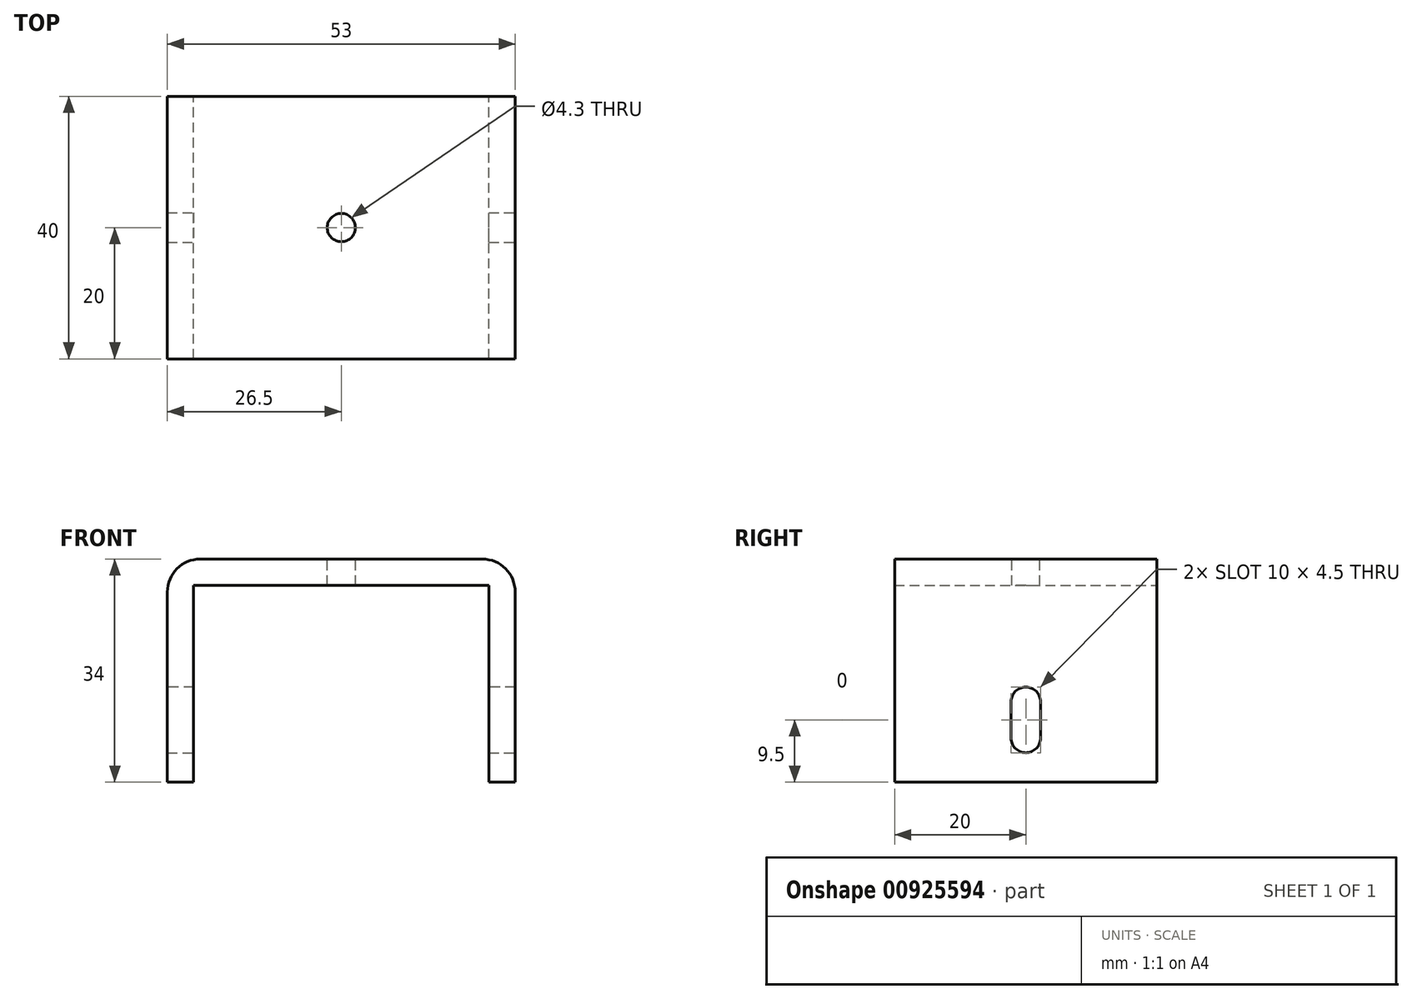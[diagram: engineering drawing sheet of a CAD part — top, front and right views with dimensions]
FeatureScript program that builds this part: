
annotation { "Feature Type Name" : "Feature", "Feature Type Description" : "" }
export const myFeature = defineFeature(function(context is Context, id is Id, definition is map)
    precondition{}
    {
        {
            var Q0;
            Q0=qCreatedBy(makeId("Front.planeOp"),FACE);
            var sketch = newSketch(context, id + "F0", { "sketchPlane" : qUnion([Q0])});
            skLineSegment(sketch, "E0.bottom", {"start": v(26.5, -17) * mm, "end": v(22.5, -17) * mm});
            skLineSegment(sketch, "E0.top", {"start": v(26.5, 17) * mm, "end": v(-26.5, 17) * mm});
            skLineSegment(sketch, "E0.left", {"start": v(26.5, -17) * mm, "end": v(26.5, 17) * mm});
            skLineSegment(sketch, "E0.right", {"start": v(-26.5, -17) * mm, "end": v(-26.5, 17) * mm});
            skPoint(sketch, "E0.middle", {"position": v(0, 0) * mm});
            skLineSegment(sketch, "E1.0", {"start": v(22.5, -17) * mm, "end": v(22.5, 13) * mm});
            skLineSegment(sketch, "E1.1", {"start": v(22.5, 13) * mm, "end": v(-22.5, 13) * mm});
            skLineSegment(sketch, "E1.2", {"start": v(-22.5, -17) * mm, "end": v(-22.5, 13) * mm});
            skLineSegment(sketch, "E2.trimOffspring", {"start": v(-22.5, -17) * mm, "end": v(-26.5, -17) * mm});
            skSolve(sketch);
        }
        {
            var Q0;
            Q0 = qSketchRegion(id + "F0", true);
            extrude(context, id + "F1", {"entities" : qUnion([Q0]), "depth" : 40 * mm, "offsetDistance" : 25 * mm});
        }
        {
            var Q0;
            Q0=makeQuery(id+"F1.opExtrude","SWEPT_EDGE",EDGE,{"disambiguationData":[OSD([sQuery(id+"F0.wireOp",EDGE,"E0.top"),sQuery(id+"F0.wireOp",EDGE,"E0.right")])]});
            var Q1;
            Q1=makeQuery(id+"F1.opExtrude","SWEPT_EDGE",EDGE,{"disambiguationData":[OSD([sQuery(id+"F0.wireOp",EDGE,"E0.top"),sQuery(id+"F0.wireOp",EDGE,"E0.left")])]});
            fillet(context, id + "F2", {"entities" : qUnion([Q0, Q1]), "radius" : 5 * mm, "tangentPropagation" : true, "allowEdgeOverflow" : false});
        }
        {
            var Q0;
            Q0=makeQuery(id+"F1.opExtrude","SWEPT_FACE",FACE,{"disambiguationData":[OSD([sQuery(id+"F0.wireOp",EDGE,"E0.top")])]});
            var sketch = newSketch(context, id + "F3", { "sketchPlane" : qUnion([Q0])});
            skCircle(sketch, "E3", {"center": v(0, -20) * mm, "radius": 2.15 * mm});
            skPoint(sketch, "E3.centerSnap0", {"position": v(21.5, -20) * mm});
            skSolve(sketch);
        }
        {
            var Q0;
            Q0 = qSketchRegion(id + "F3", true);
            extrude(context, id + "F4", {"entities" : qUnion([Q0]), "operationType" : NewBodyOperationType.REMOVE, "oppositeDirection" : true, "depth" : 25 * mm, "offsetDistance" : 25 * mm});
        }
        {
            var Q0;
            Q0=makeQuery(id+"F1.opExtrude","SWEPT_FACE",FACE,{"disambiguationData":[OSD([sQuery(id+"F0.wireOp",EDGE,"E0.left")])]});
            var sketch = newSketch(context, id + "F5", { "sketchPlane" : qUnion([Q0])});
            skLineSegment(sketch, "E4.bottom", {"start": v(-17.75, -12.5) * mm, "end": v(-22.25, -12.5) * mm});
            skLineSegment(sketch, "E4.top", {"start": v(-17.75, -2.5) * mm, "end": v(-22.25, -2.5) * mm});
            skLineSegment(sketch, "E4.left", {"start": v(-17.75, -12.5) * mm, "end": v(-17.75, -2.5) * mm});
            skLineSegment(sketch, "E4.right", {"start": v(-22.25, -12.5) * mm, "end": v(-22.25, -2.5) * mm});
            skPoint(sketch, "E4.middle", {"position": v(-20, -7.5) * mm});
            skPoint(sketch, "E4.middle.positionSnap0", {"position": v(-20, -17) * mm});
            skPoint(sketch, "E4.centerSnap0", {"position": v(-20, -17) * mm});
            skSolve(sketch);
        }
        {
            var Q0;
            Q0 = qSketchRegion(id + "F5", true);
            extrude(context, id + "F6", {"entities" : qUnion([Q0]), "operationType" : NewBodyOperationType.REMOVE, "endBound" : BoundingType.THROUGH_ALL, "oppositeDirection" : true, "depth" : 25 * mm, "offsetDistance" : 25 * mm});
        }
        {
            var Q0;
            {var subQ0=sQuery(id+"F5.wireOp",EDGE,"E4.top");var subQ1=sQuery(id+"F5.wireOp",EDGE,"E4.left");Q0=makeQuery(id+"F6.boolean.opBoolean","COPY",EDGE,{"disambiguationData":[TD([makeQuery(id+"F1.opExtrude","SWEPT_FACE",FACE,{"disambiguationData":[OSD([sQuery(id+"F0.wireOp",EDGE,"E0.left")])]})])],"derivedFrom":makeQuery(id+"F6.opExtrude","SWEPT_EDGE",EDGE,{"disambiguationData":[OSD([subQ0,subQ1])]})});}
            var Q1;
            {var subQ0=sQuery(id+"F5.wireOp",EDGE,"E4.right");var subQ1=sQuery(id+"F5.wireOp",EDGE,"E4.top");Q1=makeQuery(id+"F6.boolean.opBoolean","COPY",EDGE,{"disambiguationData":[TD([makeQuery(id+"F1.opExtrude","SWEPT_FACE",FACE,{"disambiguationData":[OSD([sQuery(id+"F0.wireOp",EDGE,"E0.left")])]})])],"derivedFrom":makeQuery(id+"F6.opExtrude","SWEPT_EDGE",EDGE,{"disambiguationData":[OSD([subQ1,subQ0])]})});}
            var Q2;
            {var subQ0=sQuery(id+"F5.wireOp",EDGE,"E4.bottom");var subQ1=sQuery(id+"F5.wireOp",EDGE,"E4.left");Q2=makeQuery(id+"F6.boolean.opBoolean","COPY",EDGE,{"disambiguationData":[TD([makeQuery(id+"F1.opExtrude","SWEPT_FACE",FACE,{"disambiguationData":[OSD([sQuery(id+"F0.wireOp",EDGE,"E0.left")])]})])],"derivedFrom":makeQuery(id+"F6.opExtrude","SWEPT_EDGE",EDGE,{"disambiguationData":[OSD([subQ0,subQ1])]})});}
            var Q3;
            {var subQ0=sQuery(id+"F5.wireOp",EDGE,"E4.bottom");var subQ1=sQuery(id+"F5.wireOp",EDGE,"E4.right");Q3=makeQuery(id+"F6.boolean.opBoolean","COPY",EDGE,{"disambiguationData":[TD([makeQuery(id+"F1.opExtrude","SWEPT_FACE",FACE,{"disambiguationData":[OSD([sQuery(id+"F0.wireOp",EDGE,"E0.left")])]})])],"derivedFrom":makeQuery(id+"F6.opExtrude","SWEPT_EDGE",EDGE,{"disambiguationData":[OSD([subQ0,subQ1])]})});}
            var Q4;
            {var subQ0=sQuery(id+"F5.wireOp",EDGE,"E4.left");var subQ1=sQuery(id+"F5.wireOp",EDGE,"E4.top");Q4=makeQuery(id+"F6.boolean.opBoolean","COPY",EDGE,{"disambiguationData":[TD([makeQuery(id+"F1.opExtrude","SWEPT_FACE",FACE,{"disambiguationData":[OSD([sQuery(id+"F0.wireOp",EDGE,"E0.right")])]})])],"derivedFrom":makeQuery(id+"F6.opExtrude","SWEPT_EDGE",EDGE,{"disambiguationData":[OSD([subQ1,subQ0])]})});}
            var Q5;
            {var subQ0=sQuery(id+"F5.wireOp",EDGE,"E4.left");var subQ1=sQuery(id+"F5.wireOp",EDGE,"E4.bottom");Q5=makeQuery(id+"F6.boolean.opBoolean","COPY",EDGE,{"disambiguationData":[TD([makeQuery(id+"F1.opExtrude","SWEPT_FACE",FACE,{"disambiguationData":[OSD([sQuery(id+"F0.wireOp",EDGE,"E0.right")])]})])],"derivedFrom":makeQuery(id+"F6.opExtrude","SWEPT_EDGE",EDGE,{"disambiguationData":[OSD([subQ1,subQ0])]})});}
            var Q6;
            {var subQ0=sQuery(id+"F5.wireOp",EDGE,"E4.top");var subQ1=sQuery(id+"F5.wireOp",EDGE,"E4.right");Q6=makeQuery(id+"F6.boolean.opBoolean","COPY",EDGE,{"disambiguationData":[TD([makeQuery(id+"F1.opExtrude","SWEPT_FACE",FACE,{"disambiguationData":[OSD([sQuery(id+"F0.wireOp",EDGE,"E0.right")])]})])],"derivedFrom":makeQuery(id+"F6.opExtrude","SWEPT_EDGE",EDGE,{"disambiguationData":[OSD([subQ0,subQ1])]})});}
            var Q7;
            {var subQ0=sQuery(id+"F5.wireOp",EDGE,"E4.bottom");var subQ1=sQuery(id+"F5.wireOp",EDGE,"E4.right");Q7=makeQuery(id+"F6.boolean.opBoolean","COPY",EDGE,{"disambiguationData":[TD([makeQuery(id+"F1.opExtrude","SWEPT_FACE",FACE,{"disambiguationData":[OSD([sQuery(id+"F0.wireOp",EDGE,"E0.right")])]})])],"derivedFrom":makeQuery(id+"F6.opExtrude","SWEPT_EDGE",EDGE,{"disambiguationData":[OSD([subQ0,subQ1])]})});}
            fillet(context, id + "F7", {"entities" : qUnion([Q0, Q1, Q2, Q3, Q4, Q5, Q6, Q7]), "radius" : 2.25 * mm, "tangentPropagation" : true, "allowEdgeOverflow" : false});
        }
    });
